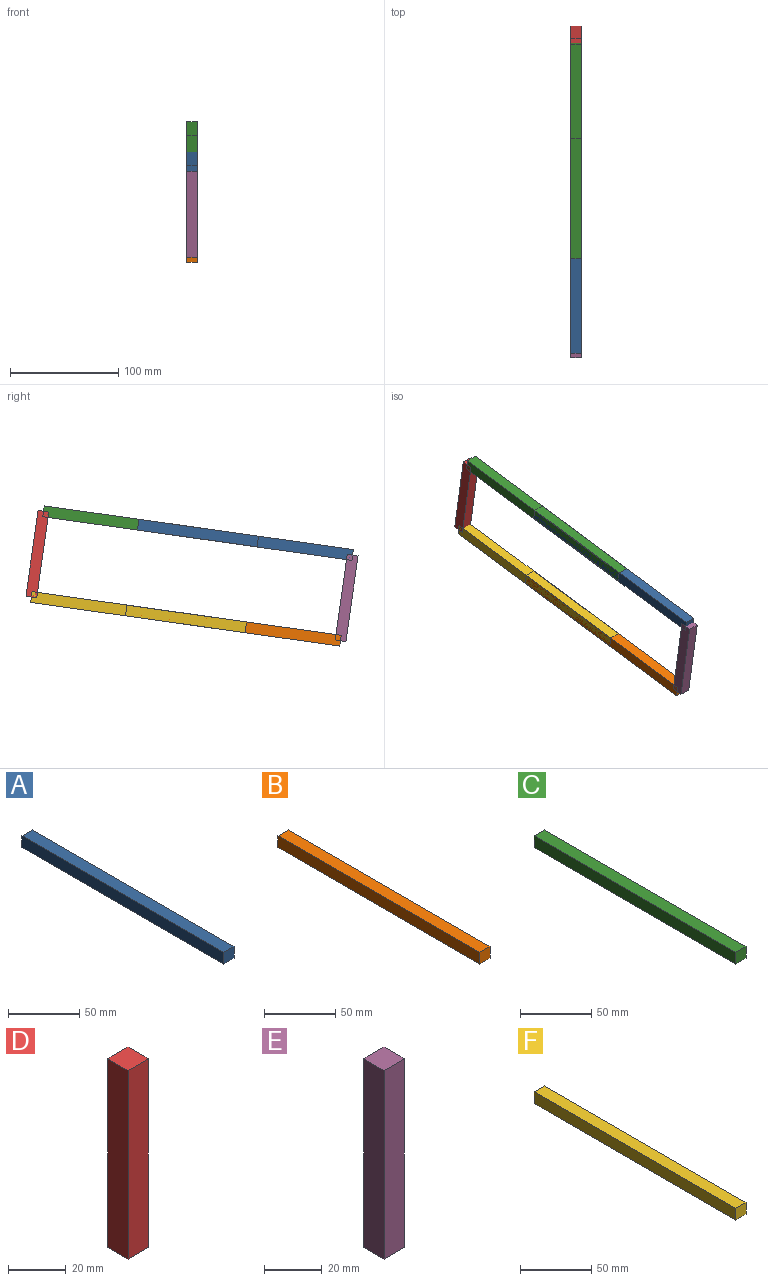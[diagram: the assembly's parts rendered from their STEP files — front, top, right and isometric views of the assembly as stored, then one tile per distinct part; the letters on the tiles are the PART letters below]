
ASSEMBLY  parts=6 mates=7
PART A: 6 faces, bbox 10x200x10 mm
  f0: plane 10x10mm, normal (0,-1,0), area 100mm2, adj f1,f3,f4,f5
  f1: plane 200x10mm, normal (0,0,-1), area 2000mm2, adj f0,f2,f4,f5
  f2: plane 10x10mm, normal (0,1,0), area 100mm2, adj f1,f3,f4,f5
  f3: plane 200x10mm, normal (0,0,1), area 2000mm2, adj f0,f2,f4,f5
  f4: plane 200x10mm, normal (1,0,0), area 2000mm2, adj f0,f1,f2,f3
  f5: plane 200x10mm, normal (-1,0,0), area 2000mm2, adj f0,f1,f2,f3
PART B: 6 faces, bbox 10x200x10 mm
  f0: plane 200x10mm, normal (0,0,1), area 2000mm2, adj f1,f3,f4,f5
  f1: plane 10x10mm, normal (0,-1,0), area 100mm2, adj f0,f2,f4,f5
  f2: plane 200x10mm, normal (0,0,-1), area 2000mm2, adj f1,f3,f4,f5
  f3: plane 10x10mm, normal (0,1,0), area 100mm2, adj f0,f2,f4,f5
  f4: plane 200x10mm, normal (1,0,0), area 2000mm2, adj f0,f1,f2,f3
  f5: plane 200x10mm, normal (-1,0,0), area 2000mm2, adj f0,f1,f2,f3
PART C: 6 faces, bbox 10x200x10 mm
  f0: plane 200x10mm, normal (0,0,-1), area 2000mm2, adj f1,f3,f4,f5
  f1: plane 10x10mm, normal (0,1,0), area 100mm2, adj f0,f2,f4,f5
  f2: plane 200x10mm, normal (0,0,1), area 2000mm2, adj f1,f3,f4,f5
  f3: plane 10x10mm, normal (0,-1,0), area 100mm2, adj f0,f2,f4,f5
  f4: plane 200x10mm, normal (1,0,0), area 2000mm2, adj f0,f1,f2,f3
  f5: plane 200x10mm, normal (-1,0,0), area 2000mm2, adj f0,f1,f2,f3
PART D: 6 faces, bbox 10x10x80 mm
  f0: plane 10x10mm, normal (0,0,1), area 100mm2, adj f1,f3,f4,f5
  f1: plane 80x10mm, normal (0,-1,0), area 800mm2, adj f0,f2,f4,f5
  f2: plane 10x10mm, normal (0,0,-1), area 100mm2, adj f1,f3,f4,f5
  f3: plane 80x10mm, normal (0,1,0), area 800mm2, adj f0,f2,f4,f5
  f4: plane 80x10mm, normal (1,0,0), area 800mm2, adj f0,f1,f2,f3
  f5: plane 80x10mm, normal (-1,0,0), area 800mm2, adj f0,f1,f2,f3
PART E: 6 faces, bbox 10x10x80 mm
  f0: plane 10x10mm, normal (0,0,1), area 100mm2, adj f1,f3,f4,f5
  f1: plane 80x10mm, normal (0,-1,0), area 800mm2, adj f0,f2,f4,f5
  f2: plane 10x10mm, normal (0,0,-1), area 100mm2, adj f1,f3,f4,f5
  f3: plane 80x10mm, normal (0,1,0), area 800mm2, adj f0,f2,f4,f5
  f4: plane 80x10mm, normal (1,0,0), area 800mm2, adj f0,f1,f2,f3
  f5: plane 80x10mm, normal (-1,0,0), area 800mm2, adj f0,f1,f2,f3
PART F: 6 faces, bbox 10x200x10 mm
  f0: plane 10x10mm, normal (0,1,0), area 100mm2, adj f1,f3,f4,f5
  f1: plane 200x10mm, normal (0,0,1), area 2000mm2, adj f0,f2,f4,f5
  f2: plane 10x10mm, normal (0,-1,0), area 100mm2, adj f1,f3,f4,f5
  f3: plane 200x10mm, normal (0,0,-1), area 2000mm2, adj f0,f2,f4,f5
  f4: plane 200x10mm, normal (1,0,0), area 2000mm2, adj f0,f1,f2,f3
  f5: plane 200x10mm, normal (-1,0,0), area 2000mm2, adj f0,f1,f2,f3
PLACE A rot(axis=(1,0,0),8deg) t=(2.13,73.03,104.61)mm
PLACE B rot(axis=(1,0,0),8deg) t=(2.13,71.63,114.52)mm
PLACE C rot(axis=(1,0,0),8deg) t=(2.13,94.64,132.05)mm
PLACE D rot(axis=(1,0,0),8deg) t=(2.13,79.08,134.9)mm
PLACE E rot(axis=(1,0,0),8deg) t=(2.13,87.19,111.66)mm
PLACE F rot(axis=(1,0,0),8deg) t=(2.13,93.24,141.95)mm
MATE revolute F.f4 <-> D.f4  axis (1,0,0) through (12.13,-440.84,7.92)mm
MATE cylindrical B.f3 <-> F.f2  axis (0,0.99,0.14) through (7.13,-528.42,-4.45)mm
MATE revolute B.f4 <-> E.f4  axis (1,0,0) through (12.13,-726.45,-32.44)mm
MATE revolute E.f4 <-> A.f4  axis (1,0,0) through (12.13,-737.64,46.78)mm
MATE revolute C.f4 <-> D.f4  axis (1,0,0) through (12.13,-452.03,87.13)mm
MATE cylindrical C.f3 <-> A.f2  axis (0,-0.99,-0.14) through (7.13,-650.07,59.15)mm
MATE slider E.f3 <-> D.f1  axis (0,0.99,0.14) through (7.13,-727.1,7.87)mm
